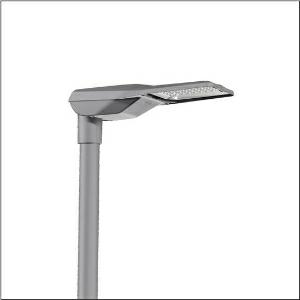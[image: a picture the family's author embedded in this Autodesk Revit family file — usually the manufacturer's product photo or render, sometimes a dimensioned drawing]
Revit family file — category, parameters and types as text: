
# Revit family: streetlight_sl_21_iq_mini___stw1_0a_5xe2e41d08gb_3fc6
name_source: partatom
category: Lighting Fixtures
units: mm (PartAtom-declared; Revit-internal decimal feet)

## family parameters
Cut with Voids When Loaded = No
Host = Face
Light Source = No
Part Type = Normal
Room Calculation Point = No
Round Connector Dimension = Use Diameter
Shared = No

## types (1)
- --- (1 x LED, 5920 lm, 37.1 W, 4000K)
    Apparent Load = 37 VA
    CIE Flux Codes = 38 75 98 100 100
    Color Rendering = 70
    Color Temperature = 4000K
    Default Elevation = 1800 mm
    Description = Streetlight SL 21 iQ mini, mast luminaire, primary light control with lens, of PMMA, primary optical cover: cover, of toughened safety glass, transparent, light distribution: STW1.0a, light emission: direct distribution, primary light characteristic: asymmetric, installation type: post-top, side-entry, LED, High Power LED, rated luminous flux: 5.920lm, luminous efficacy: 160lm/W, light colour: 740, colour temperature: 4000K, control gear: iQ-Comfort, control: Auto-Match, Temp-Guard, Lumen-Switch, Night-Set, Smart-Wire, Light-Fading, Desk-Remote (wireless, voltage-free reading and setting of iQ features in the workshop via application-optimized NFC function/RFID function), optimised constant luminous flux control (CLO 2.0), pre-setting: linear dimming characteristic, mains connection: 220..240V, AC, 50/60Hz, start of lifetime: 37W, end of service life: 39W, reduction: 18W, luminaire housing, of diecast aluminium, powder-coated, SITECO metallic grey (DB 702S), corrosivity category C5 high according to DIN EN ISO 12944, please order mast flange separately, inclination adjustable: 0°, 5°, 10°, 15°, sealing non-destructively replaceable, multi-level sealing system, length: 628mm, width: 235mm, height: 110mm, mast flange for spigot size: 42mm (side-entry): 5XC10008XM4, 60/48mm (side-entry/post-top): 5XC10108XM2, 76/60mm (side-entry/post-top): 5XC10108XM1, mounting height: 4..8m, protection rating (complete): IP66, insulation class (complete): insulation class II (safety insulation), certification: CE, ENEC, ENEC+, VDE, impact resistance: IK10, permissible operating ambient temperature for outdoor applications: -40..+50°C, standard-compliant lighting for roads and squares, packaging unit: 1 piece

Light Distribution: STW1.0a
    Height = 110 mm
    Lamp = 1 x LED
    Lamp Light Flux = 5920 lm
    Lamp Power = 37.1 W
    Lamp count = 1
    Length = 625 mm
    Luminous efficacy = 160 lm/W
    Manufacturer = Siteco
    ModVariant = No
    Model = 5XE2E41D08GB
    Number of Poles = 1
    OnlyDefault = Yes
    Power Factor = 1
    Product Name = Streetlight SL 21 iQ mini | STW1.0a
    Product group = mast luminaire | pylon top
    ProductGroupID = 6100
    Protection Class = Protection class II
    Protection Degree = IP 66
    RLX_Detail_Level = 1
    RLX_Emergency_Light_Flux = 0 lm
    RLX_Emergency_Type = 0
    RLX_Emergency_Type_DB = No
    RlxData = <blob elided: 26373 chars, md5=8a7a5e2f>
    Socket = socket
    Standby Power = 0 W
    System Light Flux = 5920 lm
    System Power = 37 W
    Type Comments = factory setting: luminous flux: 100 % | dim-lin: 254 | 385 mA
    Type Image = l_1003519.jpg
    URL = http://relux.com
    VarID = @adj_184985
    Voltage = 0 V
    Weight = 0.00 kg
    Width = 234 mm

## geometry (parser evidence)
native form markers: Blend x4, Sweep x12
no freeform markers — native parametric forms only
